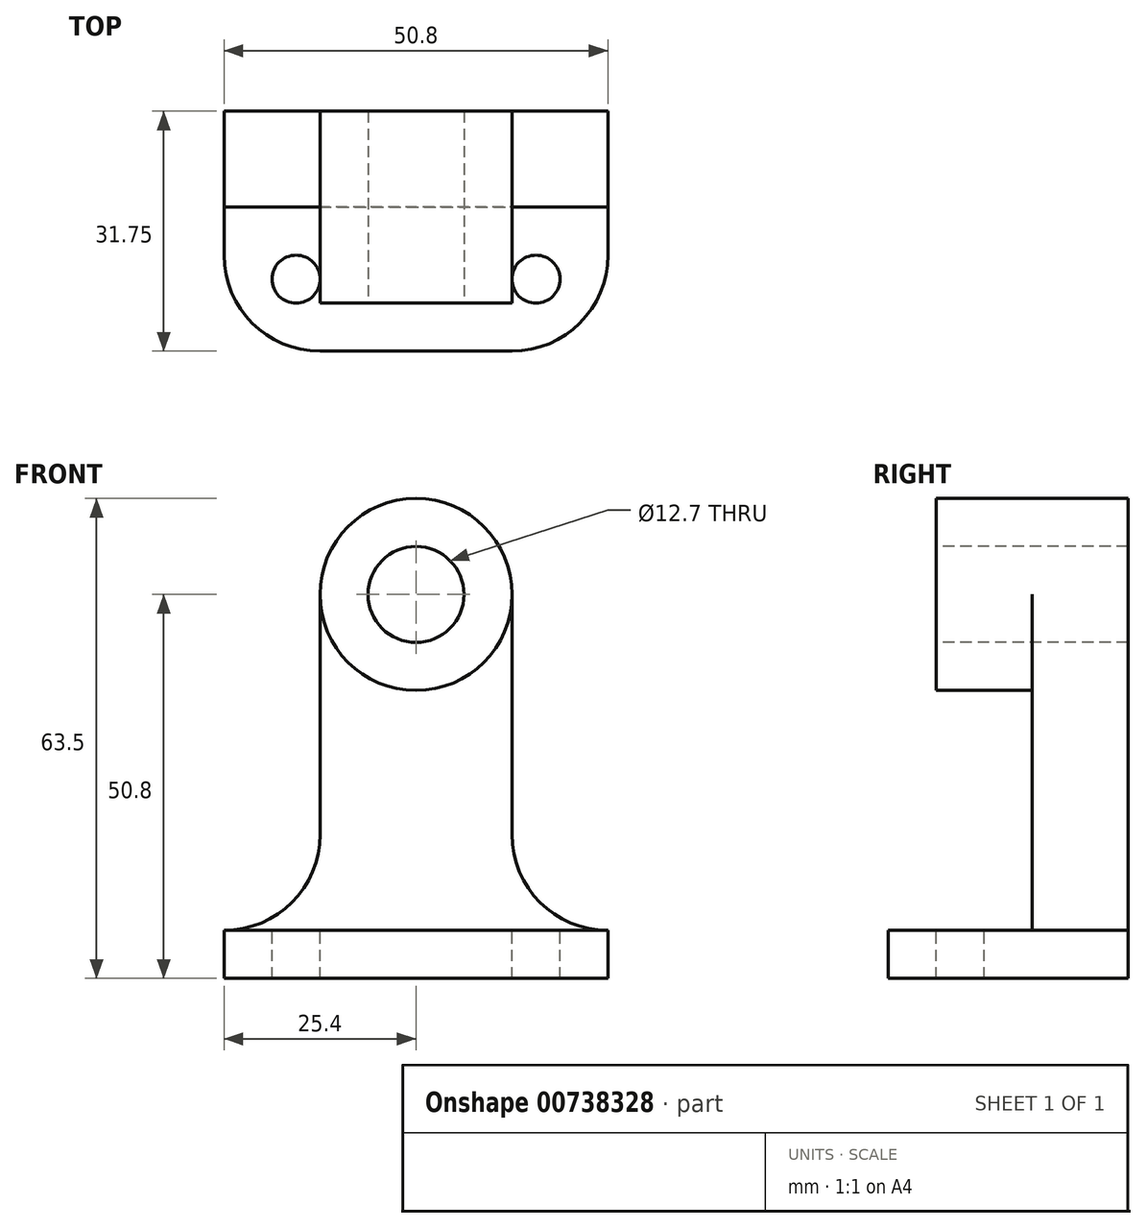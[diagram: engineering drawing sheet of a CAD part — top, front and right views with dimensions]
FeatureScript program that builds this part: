
annotation { "Feature Type Name" : "Feature", "Feature Type Description" : "" }
export const myFeature = defineFeature(function(context is Context, id is Id, definition is map)
    precondition{}
    {
        {
            var Q0;
            Q0=qCreatedBy(makeId("Right.planeOp"),FACE);
            var sketch = newSketch(context, id + "F0", { "sketchPlane" : qUnion([Q0])});
            skLineSegment(sketch, "E0", {"start": v(12.7, 63.5) * mm, "end": v(12.7, 0) * mm});
            skLineSegment(sketch, "E1", {"start": v(12.7, 0) * mm, "end": v(-19.05, 0) * mm});
            skLineSegment(sketch, "E2", {"start": v(-19.05, 0) * mm, "end": v(-19.05, 6.35) * mm});
            skLineSegment(sketch, "E3", {"start": v(-19.05, 6.35) * mm, "end": v(0, 6.35) * mm});
            skLineSegment(sketch, "E4", {"start": v(0, 6.35) * mm, "end": v(0, 63.5) * mm});
            skLineSegment(sketch, "E5", {"start": v(0, 63.5) * mm, "end": v(12.7, 63.5) * mm});
            skSolve(sketch);
        }
        {
            var Q0;
            Q0=makeQuery(id+"F0.imprint","IMPRINT",FACE,{"disambiguationData":[TD([[makeQuery(id+"F0.imprint","IMPRINT",EDGE,{"derivedFrom":sQuery(id+"F0.wireOp",EDGE,"E0")}),-1.0]])]});
            extrude(context, id + "F1", {"entities" : qUnion([Q0]), "depth" : 50.8 * mm, "offsetDistance" : 25.4 * mm});
        }
        {
            var Q0;
            Q0=makeQuery(id+"F1.opExtrude","SWEPT_FACE",FACE,{"disambiguationData":[OSD([sQuery(id+"F0.wireOp",EDGE,"E4")])]});
            var sketch = newSketch(context, id + "F2", { "sketchPlane" : qUnion([Q0])});
            skCircle(sketch, "E6", {"center": v(50.8, 19.05) * mm, "radius": 12.7 * mm});
            skCircle(sketch, "E7", {"center": v(0, 19.05) * mm, "radius": 12.7 * mm});
            skLineSegment(sketch, "E8", {"start": v(12.7, 19.05) * mm, "end": v(12.7, 63.5) * mm});
            skLineSegment(sketch, "E9", {"start": v(12.7, 63.5) * mm, "end": v(38.1, 63.5) * mm});
            skLineSegment(sketch, "E10", {"start": v(38.1, 63.5) * mm, "end": v(38.1, 19.05) * mm});
            skSolve(sketch);
        }
        {
            var Q0;
            {var subQ0=sQuery(id+"F2.wireOp",EDGE,"E8");Q0=makeQuery(id+"F2.imprint","IMPRINT",FACE,{"disambiguationData":[TD([[makeQuery(id+"F2.imprint","IMPRINT",EDGE,{"derivedFrom":subQ0}),1.0]])]});}
            var Q1;
            {var subQ0=sQuery(id+"F2.wireOp",EDGE,"E10");Q1=makeQuery(id+"F2.imprint","IMPRINT",FACE,{"disambiguationData":[TD([[makeQuery(id+"F2.imprint","IMPRINT",EDGE,{"derivedFrom":subQ0}),1.0]])]});}
            var Q2;
            {var subQ0=sQuery(id+"F2.wireOp",EDGE,"E7");var subQ1=makeQuery(id+"F2.imprint","INTERSECT",VERTEX,{"derivedFrom":[subQ0,sQuery(id+"F2.wireOp",EDGE,"E8")]});Q2=makeQuery(id+"F2.imprint","IMPRINT",FACE,{"disambiguationData":[TD([[makeQuery(id+"F2.imprint","IMPRINT",EDGE,{"disambiguationData":[TD([[subQ1,-1.0]])],"derivedFrom":subQ0}),1.0]])]});}
            var Q3;
            {var subQ0=sQuery(id+"F2.wireOp",EDGE,"E6");var subQ1=makeQuery(id+"F2.imprint","INTERSECT",VERTEX,{"derivedFrom":[subQ0,sQuery(id+"F2.wireOp",EDGE,"E10")]});Q3=makeQuery(id+"F2.imprint","IMPRINT",FACE,{"disambiguationData":[TD([[makeQuery(id+"F2.imprint","IMPRINT",EDGE,{"disambiguationData":[TD([[subQ1,1.0]])],"derivedFrom":subQ0}),1.0]])]});}
            extrude(context, id + "F3", {"entities" : qUnion([Q0, Q1, Q2, Q3]), "operationType" : NewBodyOperationType.REMOVE, "endBound" : BoundingType.THROUGH_ALL, "oppositeDirection" : true, "depth" : 25.4 * mm, "offsetDistance" : 25.4 * mm});
        }
        {
            var Q0;
            Q0=makeQuery(id+"F1.opExtrude","SWEPT_FACE",FACE,{"disambiguationData":[OSD([sQuery(id+"F0.wireOp",EDGE,"E4")])]});
            var sketch = newSketch(context, id + "F4", { "sketchPlane" : qUnion([Q0])});
            skCircle(sketch, "E11", {"center": v(25.4, 50.8) * mm, "radius": 12.7 * mm});
            skSolve(sketch);
        }
        {
            var Q0;
            {var subQ0=sQuery(id+"F4.wireOp",EDGE,"E11");var subQ2=makeQuery(id+"F4.imprint","INTERSECT",VERTEX,{"derivedFrom":[makeQuery(id+"F3.boolean.opBoolean","COPY",EDGE,{"derivedFrom":makeQuery(id+"F3.opExtrude","CAP_EDGE",EDGE,{"disambiguationData":[OSD([sQuery(id+"F2.wireOp",EDGE,"E10")])],"isStart":true})}),subQ0]});Q0=makeQuery(id+"F4.imprint","IMPRINT",FACE,{"disambiguationData":[TD([[makeQuery(id+"F4.imprint","IMPRINT",EDGE,{"disambiguationData":[TD([[subQ2,1.0]])],"derivedFrom":subQ0}),1.0]])]});}
            extrude(context, id + "F5", {"entities" : qUnion([Q0]), "operationType" : NewBodyOperationType.ADD, "depth" : 12.7 * mm, "offsetDistance" : 25.4 * mm});
        }
        {
            var Q0;
            {var subQ0=makeQuery(id+"F1.opExtrude","SWEPT_FACE",FACE,{"disambiguationData":[OSD([sQuery(id+"F0.wireOp",EDGE,"E4")])]});Q0=makeQuery(id+"F5.boolean.opBoolean","SPLIT",FACE,{"disambiguationData":[TD([subQ0,makeQuery(id+"F1.opExtrude","SWEPT_FACE",FACE,{"disambiguationData":[OSD([sQuery(id+"F0.wireOp",EDGE,"E5")])]}),makeQuery(id+"F3.boolean.opBoolean","COPY",FACE,{"derivedFrom":makeQuery(id+"F3.opExtrude","SWEPT_FACE",FACE,{"disambiguationData":[OSD([sQuery(id+"F2.wireOp",EDGE,"E8")])]})}),makeQuery(id+"F5.opExtrude","SWEPT_FACE",FACE,{"disambiguationData":[OSD([sQuery(id+"F4.wireOp",EDGE,"E11")])]})])],"derivedFrom":subQ0});}
            var Q1;
            {var subQ0=makeQuery(id+"F1.opExtrude","SWEPT_FACE",FACE,{"disambiguationData":[OSD([sQuery(id+"F0.wireOp",EDGE,"E4")])]});Q1=makeQuery(id+"F5.boolean.opBoolean","SPLIT",FACE,{"disambiguationData":[TD([subQ0,makeQuery(id+"F1.opExtrude","SWEPT_FACE",FACE,{"disambiguationData":[OSD([sQuery(id+"F0.wireOp",EDGE,"E5")])]}),makeQuery(id+"F3.boolean.opBoolean","COPY",FACE,{"derivedFrom":makeQuery(id+"F3.opExtrude","SWEPT_FACE",FACE,{"disambiguationData":[OSD([sQuery(id+"F2.wireOp",EDGE,"E10")])]})}),makeQuery(id+"F5.opExtrude","SWEPT_FACE",FACE,{"disambiguationData":[OSD([sQuery(id+"F4.wireOp",EDGE,"E11")])]})])],"derivedFrom":subQ0});}
            extrude(context, id + "F6", {"entities" : qUnion([Q0, Q1]), "operationType" : NewBodyOperationType.REMOVE, "endBound" : BoundingType.THROUGH_ALL, "oppositeDirection" : true, "depth" : 25.4 * mm, "offsetDistance" : 25.4 * mm});
        }
        {
            var Q0;
            Q0=makeQuery(id+"F5.opExtrude","CAP_FACE",FACE,{"disambiguationData":[OSD([sQuery(id+"F4.wireOp",EDGE,"E11")])],"isStart":false});
            var sketch = newSketch(context, id + "F7", { "sketchPlane" : qUnion([Q0])});
            skCircle(sketch, "E12", {"center": v(25.4, 50.8) * mm, "radius": 6.35 * mm});
            skSolve(sketch);
        }
        {
            var Q0;
            Q0=makeQuery(id+"F7.imprint","IMPRINT",FACE,{"disambiguationData":[TD([[makeQuery(id+"F7.imprint","IMPRINT",EDGE,{"derivedFrom":sQuery(id+"F7.wireOp",EDGE,"E12")}),1.0]])]});
            extrude(context, id + "F8", {"entities" : qUnion([Q0]), "operationType" : NewBodyOperationType.REMOVE, "endBound" : BoundingType.THROUGH_ALL, "oppositeDirection" : true, "depth" : 25.4 * mm, "offsetDistance" : 25.4 * mm});
        }
        {
            var Q0;
            Q0=makeQuery(id+"F1.opExtrude","SWEPT_FACE",FACE,{"disambiguationData":[OSD([sQuery(id+"F0.wireOp",EDGE,"E3")])]});
            var sketch = newSketch(context, id + "F9", { "sketchPlane" : qUnion([Q0])});
            skCircle(sketch, "E13", {"center": v(9.53, -9.53) * mm, "radius": 3.18 * mm});
            skCircle(sketch, "E14", {"center": v(41.28, -9.53) * mm, "radius": 3.18 * mm});
            skSolve(sketch);
        }
        {
            var Q0;
            Q0=makeQuery(id+"F9.imprint","IMPRINT",FACE,{"disambiguationData":[TD([[makeQuery(id+"F9.imprint","IMPRINT",EDGE,{"derivedFrom":sQuery(id+"F9.wireOp",EDGE,"E13")}),1.0]])]});
            var Q1;
            Q1=makeQuery(id+"F9.imprint","IMPRINT",FACE,{"disambiguationData":[TD([[makeQuery(id+"F9.imprint","IMPRINT",EDGE,{"derivedFrom":sQuery(id+"F9.wireOp",EDGE,"E14")}),1.0]])]});
            extrude(context, id + "F10", {"entities" : qUnion([Q0, Q1]), "operationType" : NewBodyOperationType.REMOVE, "endBound" : BoundingType.THROUGH_ALL, "oppositeDirection" : true, "depth" : 25.4 * mm, "offsetDistance" : 25.4 * mm});
        }
        {
            var Q0;
            Q0=makeQuery(id+"F1.opExtrude","SWEPT_FACE",FACE,{"disambiguationData":[OSD([sQuery(id+"F0.wireOp",EDGE,"E3")])]});
            var sketch = newSketch(context, id + "F11", { "sketchPlane" : qUnion([Q0])});
            skLineSegment(sketch, "E15", {"start": v(12.7, -19.05) * mm, "end": v(12.7, 0) * mm});
            skLineSegment(sketch, "E16", {"start": v(12.7, -19.05) * mm, "end": v(0, -19.05) * mm});
            skLineSegment(sketch, "E17", {"start": v(0, -6.35) * mm, "end": v(50.8, -6.35) * mm});
            skLineSegment(sketch, "E18", {"start": v(0, -6.35) * mm, "end": v(0, -19.05) * mm});
            skArc(sketch, "E19", {"start": v(0, -6.35) * mm, "mid": v(3.72, -15.33) * mm, "end": v(12.7, -19.05) * mm});
            skLineSegment(sketch, "E20", {"start": v(38.1, -19.05) * mm, "end": v(38.1, 0) * mm});
            skLineSegment(sketch, "E21", {"start": v(38.1, 0) * mm, "end": v(38.92, 0.42) * mm});
            skLineSegment(sketch, "E22", {"start": v(50.8, -19.05) * mm, "end": v(38.1, -19.05) * mm});
            skLineSegment(sketch, "E23", {"start": v(50.8, -19.05) * mm, "end": v(50.8, -6.35) * mm});
            skLineSegment(sketch, "E24", {"start": v(50.8, -6.35) * mm, "end": v(14.22, -6.35) * mm});
            skArc(sketch, "E25", {"start": v(38.1, -19.05) * mm, "mid": v(47.08, -15.33) * mm, "end": v(50.8, -6.35) * mm});
            skSolve(sketch);
        }
        {
            var Q0;
            Q0=makeQuery(id+"F11.imprint","IMPRINT",FACE,{"disambiguationData":[TD([[makeQuery(id+"F11.imprint","IMPRINT",EDGE,{"derivedFrom":sQuery(id+"F11.wireOp",EDGE,"E16")}),-1.0]])]});
            var Q1;
            Q1=makeQuery(id+"F11.imprint","IMPRINT",FACE,{"disambiguationData":[TD([[makeQuery(id+"F11.imprint","IMPRINT",EDGE,{"derivedFrom":sQuery(id+"F11.wireOp",EDGE,"E22")}),-1.0]])]});
            extrude(context, id + "F12", {"entities" : qUnion([Q0, Q1]), "operationType" : NewBodyOperationType.REMOVE, "endBound" : BoundingType.THROUGH_ALL, "oppositeDirection" : true, "depth" : 25.4 * mm, "offsetDistance" : 25.4 * mm});
        }
    });
